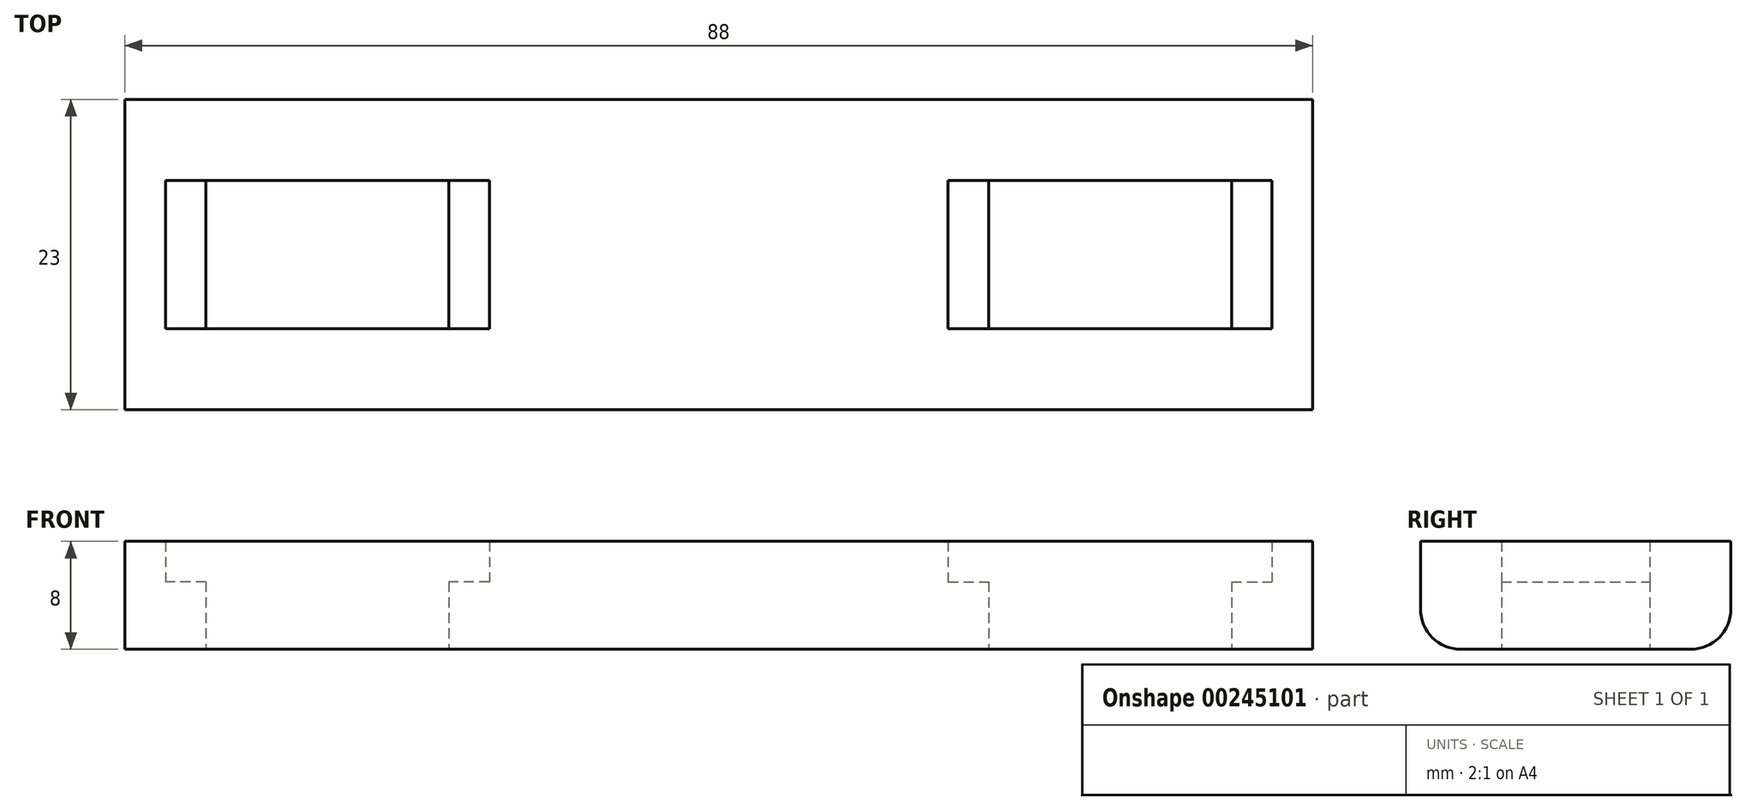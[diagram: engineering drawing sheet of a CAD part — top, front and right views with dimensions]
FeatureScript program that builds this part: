
annotation { "Feature Type Name" : "Feature", "Feature Type Description" : "" }
export const myFeature = defineFeature(function(context is Context, id is Id, definition is map)
    precondition{}
    {
        {
            var Q0;
            Q0=qCreatedBy(makeId("Top.planeOp"),FACE);
            var sketch = newSketch(context, id + "F0", { "sketchPlane" : qUnion([Q0])});
            skLineSegment(sketch, "E0", {"start": v(20, 0) * mm, "end": v(20, 5.5) * mm});
            skLineSegment(sketch, "E1", {"start": v(20, 5.5) * mm, "end": v(38, 5.5) * mm});
            skLineSegment(sketch, "E2", {"start": v(38, 5.5) * mm, "end": v(38, 0) * mm});
            skPoint(sketch, "E3", {"position": v(29, 5.5) * mm});
            skLineSegment(sketch, "E4.MirrorCS", {"start": v(20, 0) * mm, "end": v(20, -5.5) * mm});
            skLineSegment(sketch, "E5.MirrorCS", {"start": v(20, -5.5) * mm, "end": v(38, -5.5) * mm});
            skLineSegment(sketch, "E6.MirrorCS", {"start": v(38, -5.5) * mm, "end": v(38, 0) * mm});
            skLineSegment(sketch, "E7.MirrorCS", {"start": v(-20, 0) * mm, "end": v(-20, 5.5) * mm});
            skLineSegment(sketch, "E8.MirrorCS", {"start": v(-20, 0) * mm, "end": v(-20, -5.5) * mm});
            skLineSegment(sketch, "E9.MirrorCS", {"start": v(-20, 5.5) * mm, "end": v(-38, 5.5) * mm});
            skLineSegment(sketch, "E10.MirrorCS", {"start": v(-38, 5.5) * mm, "end": v(-38, 0) * mm});
            skLineSegment(sketch, "E11.MirrorCS", {"start": v(-38, -5.5) * mm, "end": v(-38, 0) * mm});
            skLineSegment(sketch, "E12.MirrorCS", {"start": v(-20, -5.5) * mm, "end": v(-38, -5.5) * mm});
            skLineSegment(sketch, "E13", {"start": v(-44, 0) * mm, "end": v(-44, 11.5) * mm});
            skLineSegment(sketch, "E14", {"start": v(-44, 11.5) * mm, "end": v(0, 11.5) * mm});
            skLineSegment(sketch, "E15.MirrorCS", {"start": v(44, 11.5) * mm, "end": v(0, 11.5) * mm});
            skLineSegment(sketch, "E16.MirrorCS", {"start": v(44, 0) * mm, "end": v(44, 11.5) * mm});
            skLineSegment(sketch, "E17.MirrorCS", {"start": v(-44, 0) * mm, "end": v(-44, -11.5) * mm});
            skLineSegment(sketch, "E18.MirrorCS", {"start": v(-44, -11.5) * mm, "end": v(0, -11.5) * mm});
            skLineSegment(sketch, "E19.MirrorCS", {"start": v(44, -11.5) * mm, "end": v(0, -11.5) * mm});
            skLineSegment(sketch, "E20.MirrorCS", {"start": v(44, 0) * mm, "end": v(44, -11.5) * mm});
            skSolve(sketch);
        }
        {
            var Q0;
            Q0 = qSketchRegion(id + "F0", true);
            extrude(context, id + "F1", {"entities" : qUnion([Q0]), "depth" : 5 * mm});
        }
        {
            var Q0;
            Q0=makeQuery(id+"F1.opExtrude","CAP_FACE",FACE,{"disambiguationData":[OSD([sQuery(id+"F0.wireOp",EDGE,"E0"),sQuery(id+"F0.wireOp",EDGE,"E1"),sQuery(id+"F0.wireOp",EDGE,"E2"),sQuery(id+"F0.wireOp",EDGE,"E4.MirrorCS"),sQuery(id+"F0.wireOp",EDGE,"E5.MirrorCS"),sQuery(id+"F0.wireOp",EDGE,"E6.MirrorCS"),sQuery(id+"F0.wireOp",EDGE,"E7.MirrorCS"),sQuery(id+"F0.wireOp",EDGE,"E8.MirrorCS"),sQuery(id+"F0.wireOp",EDGE,"E9.MirrorCS"),sQuery(id+"F0.wireOp",EDGE,"E10.MirrorCS"),sQuery(id+"F0.wireOp",EDGE,"E11.MirrorCS"),sQuery(id+"F0.wireOp",EDGE,"E12.MirrorCS"),sQuery(id+"F0.wireOp",EDGE,"E13"),sQuery(id+"F0.wireOp",EDGE,"E14"),sQuery(id+"F0.wireOp",EDGE,"E15.MirrorCS"),sQuery(id+"F0.wireOp",EDGE,"E16.MirrorCS"),sQuery(id+"F0.wireOp",EDGE,"E17.MirrorCS"),sQuery(id+"F0.wireOp",EDGE,"E18.MirrorCS"),sQuery(id+"F0.wireOp",EDGE,"E19.MirrorCS"),sQuery(id+"F0.wireOp",EDGE,"E20.MirrorCS"),sQuery(id+"F0.wireOp",EDGE,"FjZbfkwM-vOiI-KTdH-CMxk-yF9oRwshs8Dp"),sQuery(id+"F0.wireOp",EDGE,"5OlCA8ce-3Hq8-2Sao-fZ65-26pPGnPCd20i"),sQuery(id+"F0.wireOp",EDGE,"34faeb24-60f0-434d-a864-92adcd1f769e0.MirrorCS"),sQuery(id+"F0.wireOp",EDGE,"a5bf6e91-f32f-4316-8b4a-8ce11b111a2a0.MirrorCS"),sQuery(id+"F0.wireOp",EDGE,"0345fc90-6f68-4cef-bf8b-72e9aed6ccc20.MirrorCS"),sQuery(id+"F0.wireOp",EDGE,"615362c8-1d45-4ba3-99f6-920ce2a4ac7d0.MirrorCS")])],"isStart":false});
            var sketch = newSketch(context, id + "F2", { "sketchPlane" : qUnion([Q0])});
            skLineSegment(sketch, "E21", {"start": v(-38, 5.5) * mm, "end": v(-38, -5.5) * mm});
            skLineSegment(sketch, "E22", {"start": v(-38, -5.5) * mm, "end": v(-20, -5.5) * mm});
            skLineSegment(sketch, "E23", {"start": v(-20, -5.5) * mm, "end": v(-20, 5.5) * mm});
            skLineSegment(sketch, "E24", {"start": v(-20, 5.5) * mm, "end": v(-38, 5.5) * mm});
            skLineSegment(sketch, "E25", {"start": v(-44, 0) * mm, "end": v(-44, 11.5) * mm});
            skLineSegment(sketch, "E26", {"start": v(-44, 11.5) * mm, "end": v(-14, 11.5) * mm});
            skLineSegment(sketch, "E27", {"start": v(-14, 11.5) * mm, "end": v(-14, 0) * mm});
            skLineSegment(sketch, "E28", {"start": v(-17, 0) * mm, "end": v(-17, 5.5) * mm});
            skLineSegment(sketch, "E29", {"start": v(-17, 5.5) * mm, "end": v(-41, 5.5) * mm});
            skLineSegment(sketch, "E30", {"start": v(-41, 5.5) * mm, "end": v(-41, 0) * mm});
            skLineSegment(sketch, "E31.MirrorCS", {"start": v(-41, -5.5) * mm, "end": v(-41, 0) * mm});
            skLineSegment(sketch, "E32.MirrorCS", {"start": v(-17, -5.5) * mm, "end": v(-41, -5.5) * mm});
            skLineSegment(sketch, "E33.MirrorCS", {"start": v(-17, 0) * mm, "end": v(-17, -5.5) * mm});
            skLineSegment(sketch, "E34.MirrorCS", {"start": v(-14, -11.5) * mm, "end": v(-14, 0) * mm});
            skLineSegment(sketch, "E35.MirrorCS", {"start": v(-44, -11.5) * mm, "end": v(-14, -11.5) * mm});
            skLineSegment(sketch, "E36.MirrorCS", {"start": v(-44, 0) * mm, "end": v(-44, -11.5) * mm});
            skLineSegment(sketch, "E37.MirrorCS", {"start": v(17, 5.5) * mm, "end": v(41, 5.5) * mm});
            skLineSegment(sketch, "E38.MirrorCS", {"start": v(17, 0) * mm, "end": v(17, 5.5) * mm});
            skLineSegment(sketch, "E39.MirrorCS", {"start": v(17, 0) * mm, "end": v(17, -5.5) * mm});
            skLineSegment(sketch, "E40.MirrorCS", {"start": v(17, -5.5) * mm, "end": v(41, -5.5) * mm});
            skLineSegment(sketch, "E41.MirrorCS", {"start": v(41, -5.5) * mm, "end": v(41, 0) * mm});
            skLineSegment(sketch, "E42.MirrorCS", {"start": v(41, 5.5) * mm, "end": v(41, 0) * mm});
            skLineSegment(sketch, "E43.MirrorCS", {"start": v(44, 0) * mm, "end": v(44, 11.5) * mm});
            skLineSegment(sketch, "E44.MirrorCS", {"start": v(44, 11.5) * mm, "end": v(14, 11.5) * mm});
            skLineSegment(sketch, "E45.MirrorCS", {"start": v(14, 11.5) * mm, "end": v(14, 0) * mm});
            skLineSegment(sketch, "E46.MirrorCS", {"start": v(14, -11.5) * mm, "end": v(14, 0) * mm});
            skLineSegment(sketch, "E47.MirrorCS", {"start": v(44, 0) * mm, "end": v(44, -11.5) * mm});
            skLineSegment(sketch, "E48.MirrorCS", {"start": v(44, -11.5) * mm, "end": v(14, -11.5) * mm});
            skLineSegment(sketch, "E49", {"start": v(-14, 11.5) * mm, "end": v(14, 11.5) * mm});
            skLineSegment(sketch, "E50", {"start": v(14, -11.5) * mm, "end": v(-14, -11.5) * mm});
            skSolve(sketch);
        }
        {
            var Q0;
            Q0 = qSketchRegion(id + "F2", true);
            extrude(context, id + "F3", {"entities" : qUnion([Q0]), "operationType" : NewBodyOperationType.ADD, "depth" : 3 * mm});
        }
        {
            var Q0;
            Q0=makeQuery(id+"F1.opExtrude","CAP_EDGE",EDGE,{"disambiguationData":[OSD([sQuery(id+"F0.wireOp",EDGE,"E18.MirrorCS"),sQuery(id+"F0.wireOp",EDGE,"E19.MirrorCS")])],"isStart":true});
            var Q1;
            Q1=makeQuery(id+"F1.opExtrude","CAP_EDGE",EDGE,{"disambiguationData":[OSD([sQuery(id+"F0.wireOp",EDGE,"E14"),sQuery(id+"F0.wireOp",EDGE,"E15.MirrorCS")])],"isStart":true});
            fillet(context, id + "F4", {"entities" : qUnion([Q0, Q1]), "radius" : 3 * mm, "tangentPropagation" : true, "allowEdgeOverflow" : false});
        }
    });
